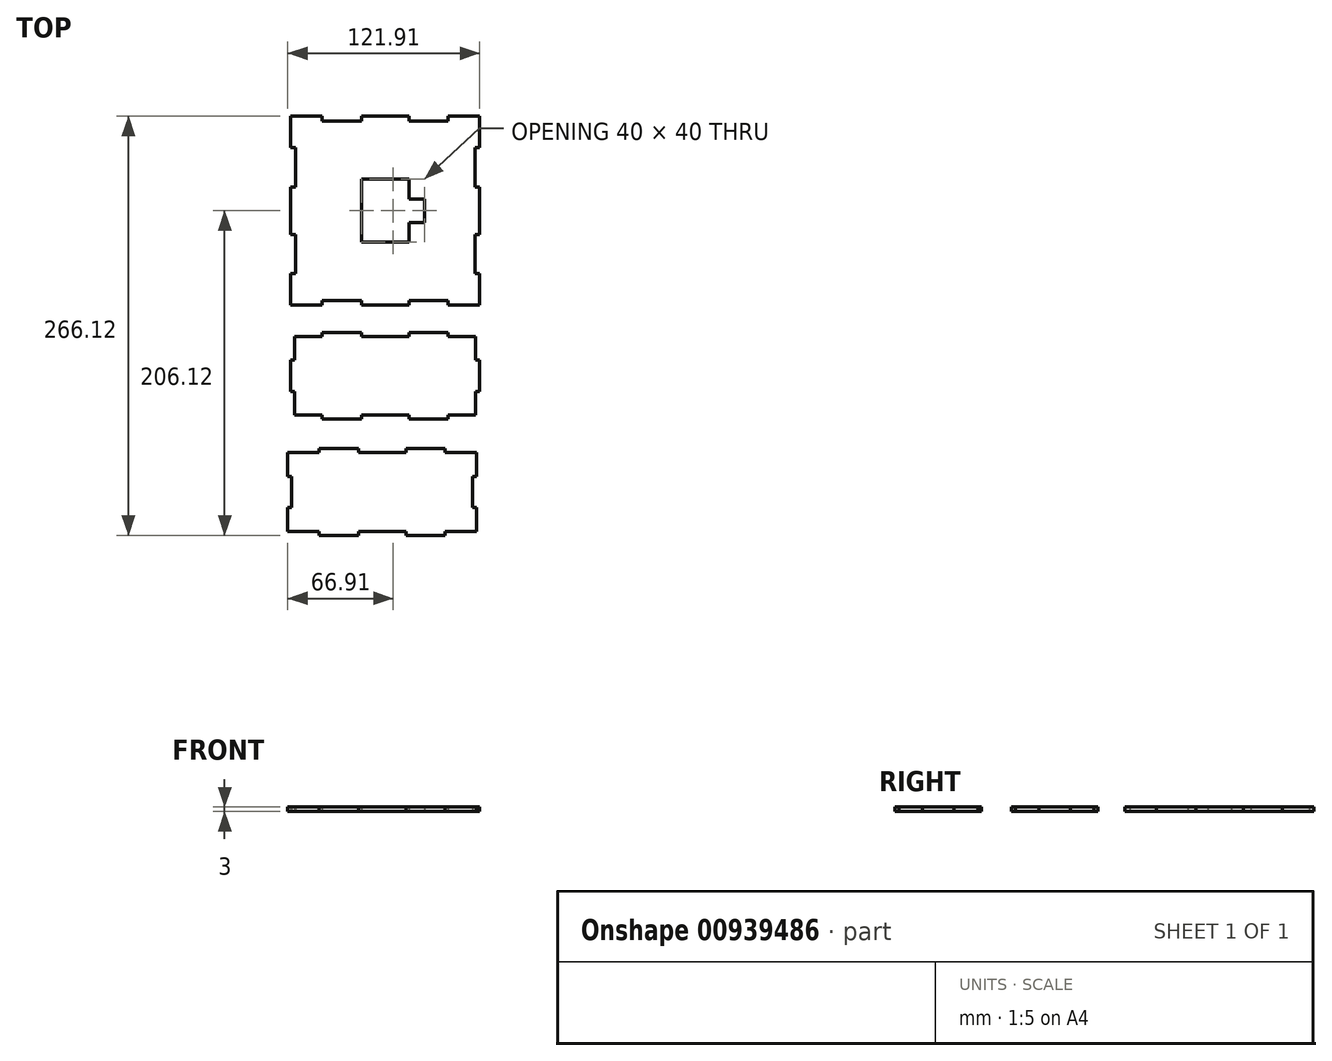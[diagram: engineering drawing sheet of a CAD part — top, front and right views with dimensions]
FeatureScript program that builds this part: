
annotation { "Feature Type Name" : "Feature", "Feature Type Description" : "" }
export const myFeature = defineFeature(function(context is Context, id is Id, definition is map)
    precondition{}
    {
        {
            var Q0;
            Q0=qCreatedBy(makeId("Top.planeOp"),FACE);
            var sketch = newSketch(context, id + "F0", { "sketchPlane" : qUnion([Q0])});
            skLineSegment(sketch, "E0.bottom", {"start": v(-60, -60) * mm, "end": v(-40, -60) * mm});
            skLineSegment(sketch, "E0.top", {"start": v(-60, 60) * mm, "end": v(-40, 60) * mm});
            skLineSegment(sketch, "E0.left", {"start": v(-60, -60) * mm, "end": v(-60, -40) * mm});
            skLineSegment(sketch, "E0.right", {"start": v(60, -60) * mm, "end": v(60, -40) * mm});
            skPoint(sketch, "E0.middle", {"position": v(0, 0) * mm});
            skLineSegment(sketch, "E1", {"start": v(-15, -60) * mm, "end": v(15, -60) * mm});
            skLineSegment(sketch, "E2", {"start": v(40, -60) * mm, "end": v(60, -60) * mm});
            skLineSegment(sketch, "E3", {"start": v(-60, -40) * mm, "end": v(-60, -60) * mm});
            skLineSegment(sketch, "E4", {"start": v(-60, -15) * mm, "end": v(-60, 15) * mm});
            skLineSegment(sketch, "E5", {"start": v(-60, 40) * mm, "end": v(-60, 60) * mm});
            skLineSegment(sketch, "E6.MirrorCS", {"start": v(60, 40) * mm, "end": v(60, 60) * mm});
            skLineSegment(sketch, "E7.MirrorCS", {"start": v(60, -15) * mm, "end": v(60, 15) * mm});
            skLineSegment(sketch, "E8.MirrorCS", {"start": v(60, -40) * mm, "end": v(60, -60) * mm});
            skLineSegment(sketch, "E9.MirrorCS", {"start": v(40, 60) * mm, "end": v(60, 60) * mm});
            skLineSegment(sketch, "E10", {"start": v(-60, -40) * mm, "end": v(-57, -40) * mm});
            skLineSegment(sketch, "E11", {"start": v(-57, -40) * mm, "end": v(-57, -15) * mm});
            skLineSegment(sketch, "E12", {"start": v(-57, -15) * mm, "end": v(-60, -15) * mm});
            skLineSegment(sketch, "E13", {"start": v(-60, 15) * mm, "end": v(-57, 15) * mm});
            skLineSegment(sketch, "E14", {"start": v(-57, 15) * mm, "end": v(-57, 40) * mm});
            skLineSegment(sketch, "E15", {"start": v(-57, 40) * mm, "end": v(-60, 40) * mm});
            skLineSegment(sketch, "E16", {"start": v(-40, 60) * mm, "end": v(-40, 57) * mm});
            skLineSegment(sketch, "E17", {"start": v(-40, 57) * mm, "end": v(-15, 57) * mm});
            skLineSegment(sketch, "E18", {"start": v(-15, 57) * mm, "end": v(-15, 60) * mm});
            skLineSegment(sketch, "E19", {"start": v(15, 60) * mm, "end": v(15, 57) * mm});
            skLineSegment(sketch, "E20", {"start": v(15, 57) * mm, "end": v(40, 57) * mm});
            skLineSegment(sketch, "E21", {"start": v(40, 57) * mm, "end": v(40, 60) * mm});
            skLineSegment(sketch, "E22.MirrorCS", {"start": v(-40, -57) * mm, "end": v(-15, -57) * mm});
            skLineSegment(sketch, "E23.MirrorCS", {"start": v(-40, -60) * mm, "end": v(-40, -57) * mm});
            skLineSegment(sketch, "E24.MirrorCS", {"start": v(-15, -57) * mm, "end": v(-15, -60) * mm});
            skLineSegment(sketch, "E25.MirrorCS", {"start": v(15, -60) * mm, "end": v(15, -57) * mm});
            skLineSegment(sketch, "E26.MirrorCS", {"start": v(15, -57) * mm, "end": v(40, -57) * mm});
            skLineSegment(sketch, "E27.MirrorCS", {"start": v(40, -57) * mm, "end": v(40, -60) * mm});
            skLineSegment(sketch, "E28.MirrorCS", {"start": v(57, 40) * mm, "end": v(60, 40) * mm});
            skLineSegment(sketch, "E29.MirrorCS", {"start": v(60, 15) * mm, "end": v(57, 15) * mm});
            skLineSegment(sketch, "E30.MirrorCS", {"start": v(57, 15) * mm, "end": v(57, 40) * mm});
            skLineSegment(sketch, "E31.MirrorCS", {"start": v(57, -15) * mm, "end": v(60, -15) * mm});
            skLineSegment(sketch, "E32.MirrorCS", {"start": v(57, -40) * mm, "end": v(57, -15) * mm});
            skLineSegment(sketch, "E33.MirrorCS", {"start": v(60, -40) * mm, "end": v(57, -40) * mm});
            skPoint(sketch, "E34.MirrorCS.end.orphan", {"position": v(60, -15) * mm});
            skPoint(sketch, "E34.MirrorCS.start.orphan", {"position": v(60, -40) * mm});
            skPoint(sketch, "E35.MirrorCS.end.orphan", {"position": v(60, 40) * mm});
            skPoint(sketch, "E35.MirrorCS.start.orphan", {"position": v(60, 15) * mm});
            skLineSegment(sketch, "E36.trimOffspring", {"start": v(-15, 60) * mm, "end": v(15, 60) * mm});
            skLineSegment(sketch, "E37.bottom", {"start": v(-15, -20) * mm, "end": v(15, -20) * mm});
            skLineSegment(sketch, "E37.top", {"start": v(-15, 20) * mm, "end": v(15, 20) * mm});
            skLineSegment(sketch, "E37.left", {"start": v(-15, -20) * mm, "end": v(-15, 20) * mm});
            skLineSegment(sketch, "E37.right", {"start": v(15, -20) * mm, "end": v(15, -7.5) * mm});
            skLineSegment(sketch, "E38.bottom", {"start": v(25, -7.5) * mm, "end": v(15, -7.5) * mm});
            skLineSegment(sketch, "E38.top", {"start": v(25, 7.5) * mm, "end": v(15, 7.5) * mm});
            skLineSegment(sketch, "E38.left", {"start": v(25, -7.5) * mm, "end": v(25, 7.5) * mm});
            skPoint(sketch, "E38.middle", {"position": v(15, 0) * mm});
            skPoint(sketch, "E38.right.end.orphan", {"position": v(5, 7.5) * mm});
            skPoint(sketch, "E39.orphan", {"position": v(5, -7.5) * mm});
            skLineSegment(sketch, "E40.trimOffspring", {"start": v(15, 7.5) * mm, "end": v(15, 20) * mm});
            skSolve(sketch);
        }
        {
            var Q0;
            Q0 = qSketchRegion(id + "F0", true);
            extrude(context, id + "F1", {"entities" : qUnion([Q0]), "depth" : 3 * mm, "offsetDistance" : 25 * mm});
        }
        {
            var Q0;
            Q0=qCreatedBy(makeId("Top.planeOp"),FACE);
            var sketch = newSketch(context, id + "F2", { "sketchPlane" : qUnion([Q0])});
            skLineSegment(sketch, "E41.bottom", {"start": v(-40, -132.29) * mm, "end": v(-15, -132.29) * mm});
            skLineSegment(sketch, "E41.top", {"start": v(-40, -77.29) * mm, "end": v(-15, -77.29) * mm});
            skLineSegment(sketch, "E41.right", {"start": v(60, -114.79) * mm, "end": v(60, -94.79) * mm});
            skPoint(sketch, "E41.middle", {"position": v(0, -104.79) * mm});
            skLineSegment(sketch, "E42", {"start": v(-60, -94.79) * mm, "end": v(-60, -114.79) * mm});
            skLineSegment(sketch, "E43", {"start": v(15, -77.29) * mm, "end": v(40, -77.29) * mm});
            skLineSegment(sketch, "E44", {"start": v(-40, -77.29) * mm, "end": v(-40, -79.79) * mm});
            skLineSegment(sketch, "E45", {"start": v(-40, -79.79) * mm, "end": v(-57.5, -79.79) * mm});
            skLineSegment(sketch, "E46", {"start": v(-15, -77.29) * mm, "end": v(-15, -79.79) * mm});
            skLineSegment(sketch, "E47", {"start": v(-15, -79.79) * mm, "end": v(15, -79.79) * mm});
            skLineSegment(sketch, "E48", {"start": v(15, -79.79) * mm, "end": v(15, -77.29) * mm});
            skLineSegment(sketch, "E49", {"start": v(40, -77.29) * mm, "end": v(40, -79.79) * mm});
            skLineSegment(sketch, "E50", {"start": v(40, -79.79) * mm, "end": v(57.5, -79.79) * mm});
            skLineSegment(sketch, "E51", {"start": v(-60, -94.79) * mm, "end": v(-57.5, -94.79) * mm});
            skLineSegment(sketch, "E52", {"start": v(-57.5, -94.79) * mm, "end": v(-57.5, -79.79) * mm});
            skLineSegment(sketch, "E53", {"start": v(-60, -114.79) * mm, "end": v(-57.5, -114.79) * mm});
            skLineSegment(sketch, "E54", {"start": v(-57.5, -114.79) * mm, "end": v(-57.5, -129.79) * mm});
            skLineSegment(sketch, "E55.MirrorCS", {"start": v(-40, -129.79) * mm, "end": v(-57.5, -129.79) * mm});
            skLineSegment(sketch, "E56.MirrorCS", {"start": v(-40, -132.29) * mm, "end": v(-40, -129.79) * mm});
            skLineSegment(sketch, "E57.MirrorCS", {"start": v(-15, -132.29) * mm, "end": v(-15, -129.79) * mm});
            skLineSegment(sketch, "E58.MirrorCS", {"start": v(-15, -129.79) * mm, "end": v(15, -129.79) * mm});
            skLineSegment(sketch, "E59.MirrorCS", {"start": v(15, -129.79) * mm, "end": v(15, -132.29) * mm});
            skLineSegment(sketch, "E60.MirrorCS", {"start": v(40, -132.29) * mm, "end": v(40, -129.79) * mm});
            skLineSegment(sketch, "E61.MirrorCS", {"start": v(40, -129.79) * mm, "end": v(57.5, -129.79) * mm});
            skLineSegment(sketch, "E62.MirrorCS", {"start": v(57.5, -114.79) * mm, "end": v(57.5, -129.79) * mm});
            skLineSegment(sketch, "E63.MirrorCS", {"start": v(60, -114.79) * mm, "end": v(57.5, -114.79) * mm});
            skLineSegment(sketch, "E64.MirrorCS", {"start": v(60, -94.79) * mm, "end": v(57.5, -94.79) * mm});
            skLineSegment(sketch, "E65.MirrorCS", {"start": v(57.5, -94.79) * mm, "end": v(57.5, -79.79) * mm});
            skLineSegment(sketch, "E66.top", {"start": v(-41.91, -151.12) * mm, "end": v(-16.91, -151.12) * mm});
            skLineSegment(sketch, "E66.left", {"start": v(-61.91, -203.62) * mm, "end": v(-61.91, -188.62) * mm});
            skLineSegment(sketch, "E66.right", {"start": v(58.09, -203.62) * mm, "end": v(58.09, -188.62) * mm});
            skPoint(sketch, "E66.middle", {"position": v(-1.91, -178.62) * mm});
            skLineSegment(sketch, "E67", {"start": v(-61.91, -153.62) * mm, "end": v(-61.91, -168.62) * mm});
            skLineSegment(sketch, "E68", {"start": v(-61.91, -188.62) * mm, "end": v(-61.91, -203.62) * mm});
            skLineSegment(sketch, "E69", {"start": v(13.09, -151.12) * mm, "end": v(38.09, -151.12) * mm});
            skLineSegment(sketch, "E70", {"start": v(-41.91, -151.12) * mm, "end": v(-41.91, -153.62) * mm});
            skLineSegment(sketch, "E71", {"start": v(-41.91, -153.62) * mm, "end": v(-61.91, -153.62) * mm});
            skLineSegment(sketch, "E72", {"start": v(-16.91, -151.12) * mm, "end": v(-16.91, -153.62) * mm});
            skLineSegment(sketch, "E73", {"start": v(-16.91, -153.62) * mm, "end": v(13.09, -153.62) * mm});
            skLineSegment(sketch, "E74", {"start": v(13.09, -153.62) * mm, "end": v(13.09, -151.12) * mm});
            skLineSegment(sketch, "E75", {"start": v(38.09, -151.12) * mm, "end": v(38.09, -153.62) * mm});
            skLineSegment(sketch, "E76", {"start": v(38.09, -153.62) * mm, "end": v(58.09, -153.62) * mm});
            skLineSegment(sketch, "E77", {"start": v(-61.91, -168.62) * mm, "end": v(-59.41, -168.62) * mm});
            skLineSegment(sketch, "E78", {"start": v(-61.91, -188.62) * mm, "end": v(-59.41, -188.62) * mm});
            skLineSegment(sketch, "E79.MirrorCS", {"start": v(-41.91, -203.62) * mm, "end": v(-61.91, -203.62) * mm});
            skLineSegment(sketch, "E80.MirrorCS", {"start": v(-41.91, -206.12) * mm, "end": v(-41.91, -203.62) * mm});
            skLineSegment(sketch, "E81.MirrorCS", {"start": v(-16.91, -206.12) * mm, "end": v(-16.91, -203.62) * mm});
            skLineSegment(sketch, "E82.MirrorCS", {"start": v(-16.91, -203.62) * mm, "end": v(13.09, -203.62) * mm});
            skLineSegment(sketch, "E83.MirrorCS", {"start": v(13.09, -203.62) * mm, "end": v(13.09, -206.12) * mm});
            skLineSegment(sketch, "E84.MirrorCS", {"start": v(38.09, -206.12) * mm, "end": v(38.09, -203.62) * mm});
            skLineSegment(sketch, "E85.MirrorCS", {"start": v(38.09, -203.62) * mm, "end": v(58.09, -203.62) * mm});
            skLineSegment(sketch, "E86.MirrorCS", {"start": v(58.09, -188.62) * mm, "end": v(55.59, -188.62) * mm});
            skLineSegment(sketch, "E87.MirrorCS", {"start": v(58.09, -168.62) * mm, "end": v(55.59, -168.62) * mm});
            skPoint(sketch, "E88.trimOffspring.end.orphan", {"position": v(60, -77.29) * mm});
            skPoint(sketch, "E89.orphan", {"position": v(60, -79.79) * mm});
            skPoint(sketch, "E90.orphan", {"position": v(-60, -77.29) * mm});
            skPoint(sketch, "E91.orphan", {"position": v(-60, -79.79) * mm});
            skLineSegment(sketch, "E92.trimOffspring", {"start": v(-60, -114.79) * mm, "end": v(-60, -94.79) * mm});
            skPoint(sketch, "E93.orphan", {"position": v(-60, -132.29) * mm});
            skLineSegment(sketch, "E94.trimOffspring", {"start": v(15, -132.29) * mm, "end": v(40, -132.29) * mm});
            skPoint(sketch, "E95.orphan", {"position": v(60, -132.29) * mm});
            skLineSegment(sketch, "E96", {"start": v(-59.41, -168.62) * mm, "end": v(-59.41, -188.62) * mm});
            skLineSegment(sketch, "E97", {"start": v(55.59, -168.62) * mm, "end": v(55.59, -188.62) * mm});
            skPoint(sketch, "E98.orphan", {"position": v(-61.91, -151.12) * mm});
            skLineSegment(sketch, "E99.trimOffspring", {"start": v(-61.91, -168.62) * mm, "end": v(-61.91, -153.62) * mm});
            skLineSegment(sketch, "E100.trimOffspring", {"start": v(-41.91, -206.12) * mm, "end": v(-16.91, -206.12) * mm});
            skPoint(sketch, "E101.orphan", {"position": v(-61.91, -206.12) * mm});
            skPoint(sketch, "E102.end.orphan", {"position": v(-59.41, -153.62) * mm});
            skLineSegment(sketch, "E103.trimOffspring", {"start": v(13.09, -206.12) * mm, "end": v(38.09, -206.12) * mm});
            skPoint(sketch, "E104.orphan", {"position": v(58.09, -206.12) * mm});
            skLineSegment(sketch, "E105.trimOffspring", {"start": v(58.09, -168.62) * mm, "end": v(58.09, -153.62) * mm});
            skPoint(sketch, "E106.orphan", {"position": v(58.09, -151.12) * mm});
            skSolve(sketch);
        }
        {
            var Q0;
            Q0 = qSketchRegion(id + "F2", true);
            extrude(context, id + "F3", {"entities" : qUnion([Q0]), "depth" : 3 * mm, "offsetDistance" : 25 * mm});
        }
    });
